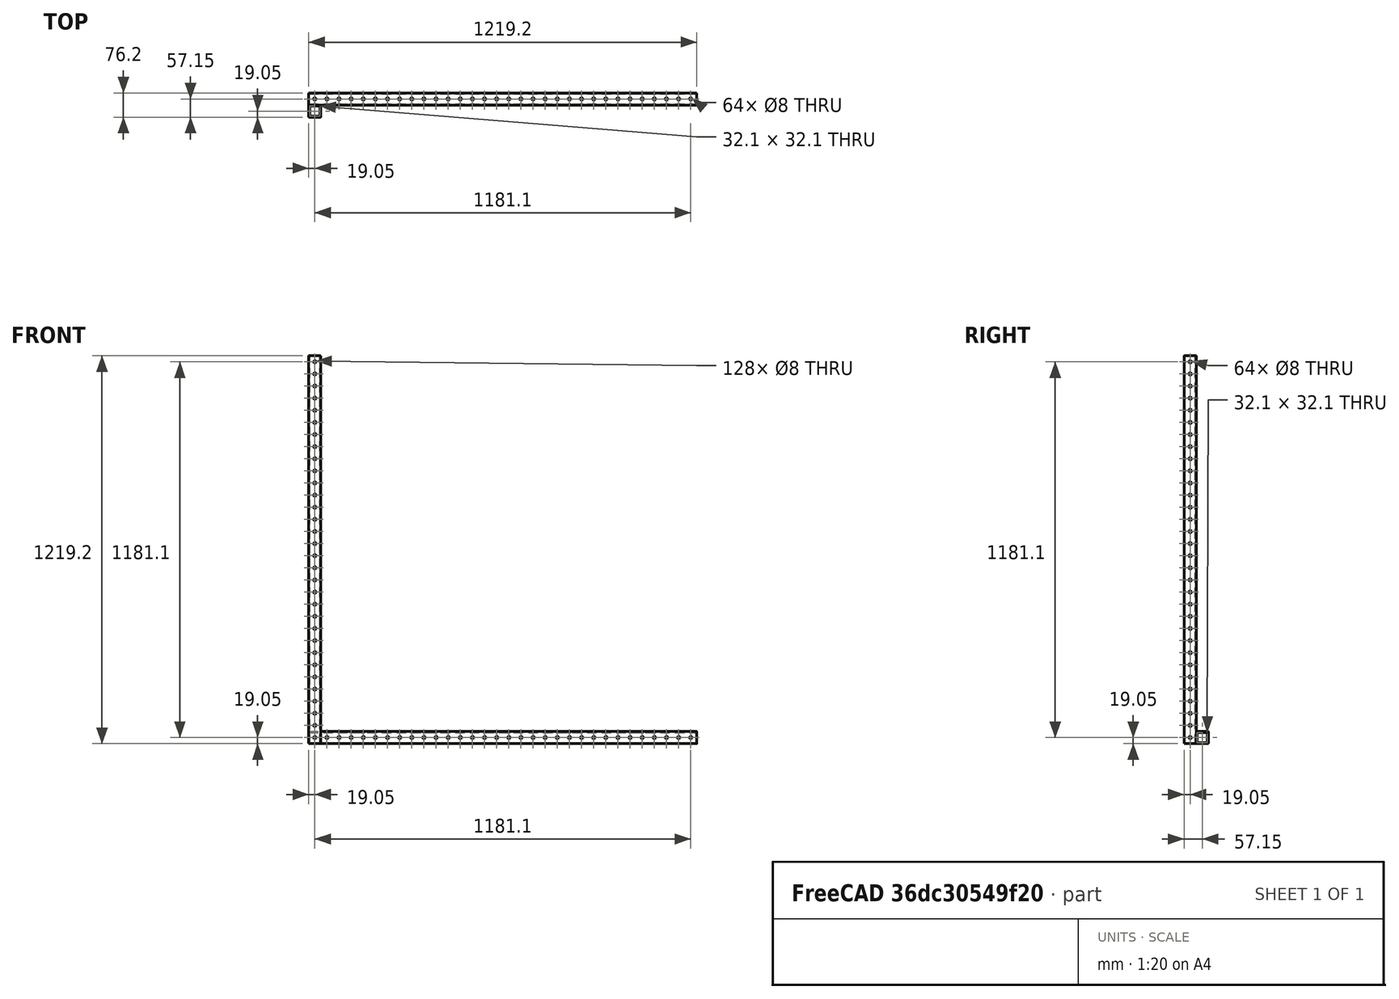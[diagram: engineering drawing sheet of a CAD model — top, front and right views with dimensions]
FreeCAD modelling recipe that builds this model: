
FCSTD DOCUMENT  (FreeCAD 0.15R4671 (Git))
Label: desk
License: All rights reserved
LicenseURL: http://en.wikipedia.org/wiki/All_rights_reserved
objects: Part::Cut×6, Part::Box×4, Part::Cylinder×4, Part::FeaturePython×4, PartDesign::Fillet×2
note: 20 computed .brp shape members not serialized (recipe doc carries the construction recipe); baked Part::Feature solids carry a one-line shape summary decoded from their .brp

FEATURE [Part::Box] Box  label="Beam"
  Height = 1219.2
  Length = 38.1
  Width = 38.1
FEATURE [Part::Cylinder] Cylinder
  Angle = 360
  Height = 38.1
  Placement = pos=(0,19.05,19.05) rot=(0,1,0;1.5708rad)
  Radius = 4
FEATURE [Part::Cylinder] Cylinder001
  Angle = 360
  Height = 38.1
  Placement = pos=(19.05,38.1,19.05) rot=(1,0,0;1.5708rad)
  Radius = 4
FEATURE [Part::FeaturePython] Array  label="Holes1"  # Draft array (typed FeaturePython)
  Angle = 360
  ArrayType = 0
  Axis = (0,0,1)
  Base = -> Cylinder001
  Center = (0,0,0)
  Fuse = false
  IntervalAxis = (0,0,0)
  IntervalX = (1,0,0)
  IntervalY = (0,1,0)
  IntervalZ = (0,0,38.1)
  NumberPolar = 1
  NumberX = 1
  NumberY = 1
  NumberZ = 32
FEATURE [Part::FeaturePython] Array001  label="Holes2"  # Draft array (typed FeaturePython)
  Angle = 360
  ArrayType = 0
  Axis = (0,0,1)
  Base = -> Cylinder
  Center = (0,0,0)
  Fuse = false
  IntervalAxis = (0,0,0)
  IntervalX = (1,0,0)
  IntervalY = (0,1,0)
  IntervalZ = (0,0,38.1)
  NumberPolar = 1
  NumberX = 1
  NumberY = 1
  NumberZ = 32
FEATURE [Part::Box] Box001  label="Cutout"
  Height = 1219.2
  Length = 32.1
  Placement = pos=(3,3,0) rot=(0,0,1;0rad)
  Width = 32.1
FEATURE [Part::Cut] Cut
  Base = -> Box
  Tool = -> Array
FEATURE [Part::Cut] Cut001
  Base = -> Cut
  Tool = -> Array001
FEATURE [Part::Cut] Cut002
  Base = -> Cut001
  Placement = pos=(0,38.1,38.1) rot=(0,1,0;1.5708rad)
  Tool = -> Box001
FEATURE [PartDesign::Fillet] Fillet
  Base = -> Cut002 [Edge84,Edge38,Edge4,Edge1]
  Placement = pos=(0,38.1,38.1) rot=(0,1,0;1.5708rad)
  Radius = 1
FEATURE [Part::Box] Box002  label="Beam001"
  Height = 1219.2
  Length = 38.1
  Width = 38.1
FEATURE [Part::Cylinder] Cylinder002
  Angle = 360
  Height = 38.1
  Placement = pos=(0,19.05,19.05) rot=(0,1,0;1.5708rad)
  Radius = 4
FEATURE [Part::Cylinder] Cylinder003
  Angle = 360
  Height = 38.1
  Placement = pos=(19.05,38.1,19.05) rot=(1,0,0;1.5708rad)
  Radius = 4
FEATURE [Part::FeaturePython] Array002  label="Holes003"  # Draft array (typed FeaturePython)
  Angle = 360
  ArrayType = 0
  Axis = (0,0,1)
  Base = -> Cylinder003
  Center = (0,0,0)
  Fuse = false
  IntervalAxis = (0,0,0)
  IntervalX = (1,0,0)
  IntervalY = (0,1,0)
  IntervalZ = (0,0,38.1)
  NumberPolar = 1
  NumberX = 1
  NumberY = 1
  NumberZ = 32
FEATURE [Part::FeaturePython] Array003  label="Holes004"  # Draft array (typed FeaturePython)
  Angle = 360
  ArrayType = 0
  Axis = (0,0,1)
  Base = -> Cylinder002
  Center = (0,0,0)
  Fuse = false
  IntervalAxis = (0,0,0)
  IntervalX = (1,0,0)
  IntervalY = (0,1,0)
  IntervalZ = (0,0,38.1)
  NumberPolar = 1
  NumberX = 1
  NumberY = 1
  NumberZ = 32
FEATURE [Part::Box] Box003  label="Cutout001"
  Height = 1219.2
  Length = 32.1
  Placement = pos=(3,3,0) rot=(0,0,1;0rad)
  Width = 32.1
FEATURE [Part::Cut] Cut003
  Base = -> Box002
  Tool = -> Array002
FEATURE [Part::Cut] Cut004
  Base = -> Cut003
  Tool = -> Array003
FEATURE [Part::Cut] Cut005
  Base = -> Cut004
  Tool = -> Box003
FEATURE [PartDesign::Fillet] Fillet001
  Base = -> Cut005 [Edge84,Edge38,Edge4,Edge1]
  Radius = 1
